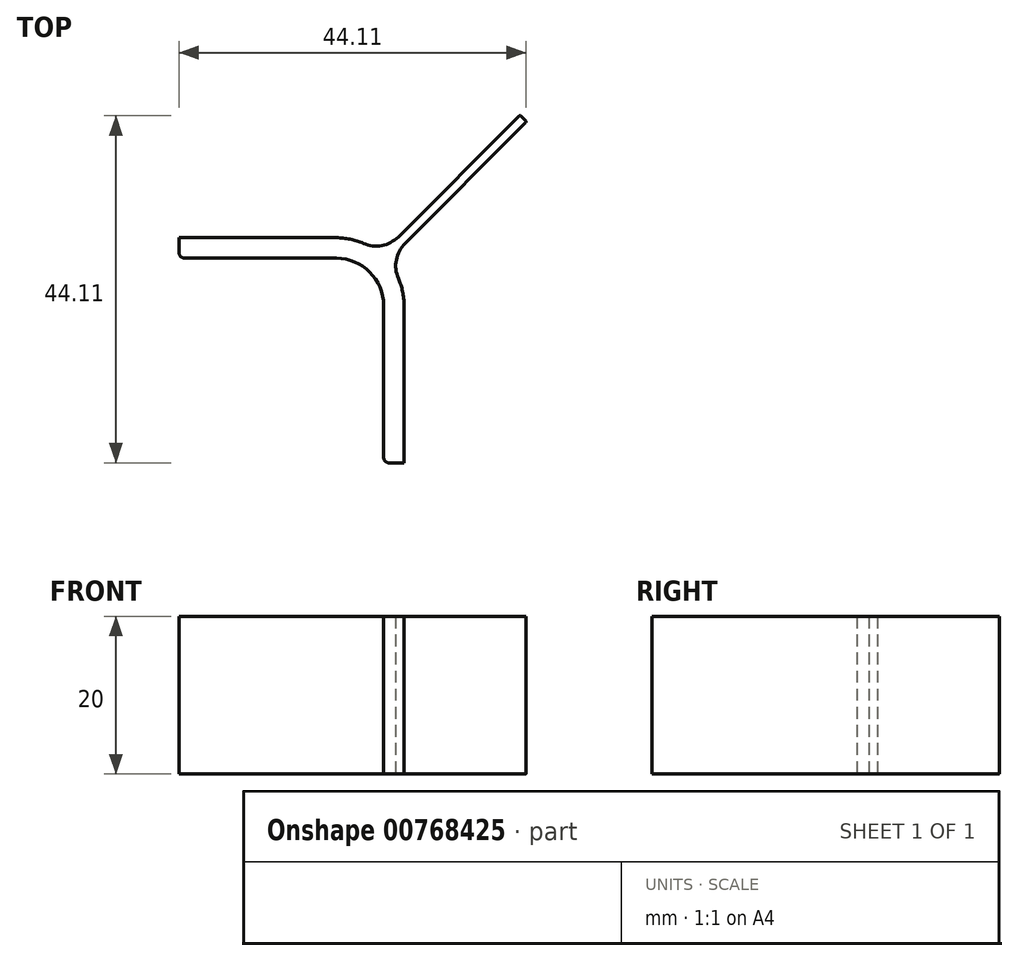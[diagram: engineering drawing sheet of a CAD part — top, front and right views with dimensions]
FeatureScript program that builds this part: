
annotation { "Feature Type Name" : "Feature", "Feature Type Description" : "" }
export const myFeature = defineFeature(function(context is Context, id is Id, definition is map)
    precondition{}
    {
        {
            var Q0;
            Q0=qCreatedBy(makeId("Top.planeOp"),FACE);
            var sketch = newSketch(context, id + "F0", { "sketchPlane" : qUnion([Q0])});
            skArc(sketch, "E0", {"start": v(6, 0) * mm, "mid": v(4.24, 4.24) * mm, "end": v(0, 6) * mm});
            skLineSegment(sketch, "E1", {"start": v(0, 6) * mm, "end": v(-19.25, 6) * mm});
            skLineSegment(sketch, "E2", {"start": v(6, 0) * mm, "end": v(6, -19.25) * mm});
            skLineSegment(sketch, "E3.0", {"start": v(0, 8.6) * mm, "end": v(-20, 8.6) * mm});
            skArc(sketch, "E3.1", {"start": v(8.6, 0) * mm, "mid": v(8.42, 1.76) * mm, "end": v(7.88, 3.44) * mm});
            skLineSegment(sketch, "E3.2", {"start": v(8.6, 0) * mm, "end": v(8.6, -20) * mm});
            skLineSegment(sketch, "E4", {"start": v(-20, 6.75) * mm, "end": v(-20, 8.6) * mm});
            skLineSegment(sketch, "E5", {"start": v(6.75, -20) * mm, "end": v(8.6, -20) * mm});
            skLineSegment(sketch, "E6", {"start": v(0, 0) * mm, "end": v(6.08, 6.08) * mm, "construction": true});
            skLineSegment(sketch, "E7", {"start": v(6.08, 6.08) * mm, "end": v(23.76, 23.76) * mm, "construction": true});
            skLineSegment(sketch, "E8.0", {"start": v(8.72, 7.87) * mm, "end": v(24.06, 23.21) * mm});
            skLineSegment(sketch, "E9.MirrorCS", {"start": v(7.87, 8.72) * mm, "end": v(23.21, 24.06) * mm});
            skPoint(sketch, "E10.orphan", {"position": v(4.67, 3.82) * mm});
            skPoint(sketch, "E11.orphan", {"position": v(3.82, 4.67) * mm});
            skLineSegment(sketch, "E12", {"start": v(24.06, 23.46) * mm, "end": v(23.76, 23.76) * mm});
            skLineSegment(sketch, "E13", {"start": v(23.76, 23.76) * mm, "end": v(23.46, 24.06) * mm});
            skArc(sketch, "E14.trimOffspring", {"start": v(3.44, 7.88) * mm, "mid": v(1.76, 8.42) * mm, "end": v(0, 8.6) * mm});
            skPoint(sketch, "E15.visualSharp", {"position": v(6.5, 5.64) * mm});
            skArc(sketch, "E15.filletArc", {"start": v(8.72, 7.87) * mm, "mid": v(7.62, 5.78) * mm, "end": v(7.88, 3.44) * mm});
            skPoint(sketch, "E16.visualSharp", {"position": v(5.64, 6.5) * mm});
            skArc(sketch, "E16.filletArc", {"start": v(3.44, 7.88) * mm, "mid": v(5.78, 7.62) * mm, "end": v(7.87, 8.72) * mm});
            skPoint(sketch, "E17.visualSharp", {"position": v(23.33, 24.18) * mm});
            skArc(sketch, "E17.filletArc", {"start": v(23.46, 24.06) * mm, "mid": v(23.33, 24.11) * mm, "end": v(23.21, 24.06) * mm});
            skPoint(sketch, "E18.visualSharp", {"position": v(24.18, 23.33) * mm});
            skArc(sketch, "E18.filletArc", {"start": v(24.06, 23.21) * mm, "mid": v(24.11, 23.33) * mm, "end": v(24.06, 23.46) * mm});
            skPoint(sketch, "E19.visualSharp", {"position": v(6, -20) * mm});
            skArc(sketch, "E19.filletArc", {"start": v(6, -19.25) * mm, "mid": v(6.22, -19.78) * mm, "end": v(6.75, -20) * mm});
            skPoint(sketch, "E20.visualSharp", {"position": v(-20, 6) * mm});
            skArc(sketch, "E20.filletArc", {"start": v(-20, 6.75) * mm, "mid": v(-19.78, 6.22) * mm, "end": v(-19.25, 6) * mm});
            skSolve(sketch);
        }
        {
            var Q0;
            Q0=makeQuery(id+"F0.imprint","IMPRINT",FACE,{"disambiguationData":[TD([[makeQuery(id+"F0.imprint","IMPRINT",EDGE,{"derivedFrom":sQuery(id+"F0.wireOp",EDGE,"E0")}),-1.0]])]});
            extrude(context, id + "F1", {"entities" : qUnion([Q0]), "depth" : 20 * mm, "offsetDistance" : 25 * mm});
        }
    });
